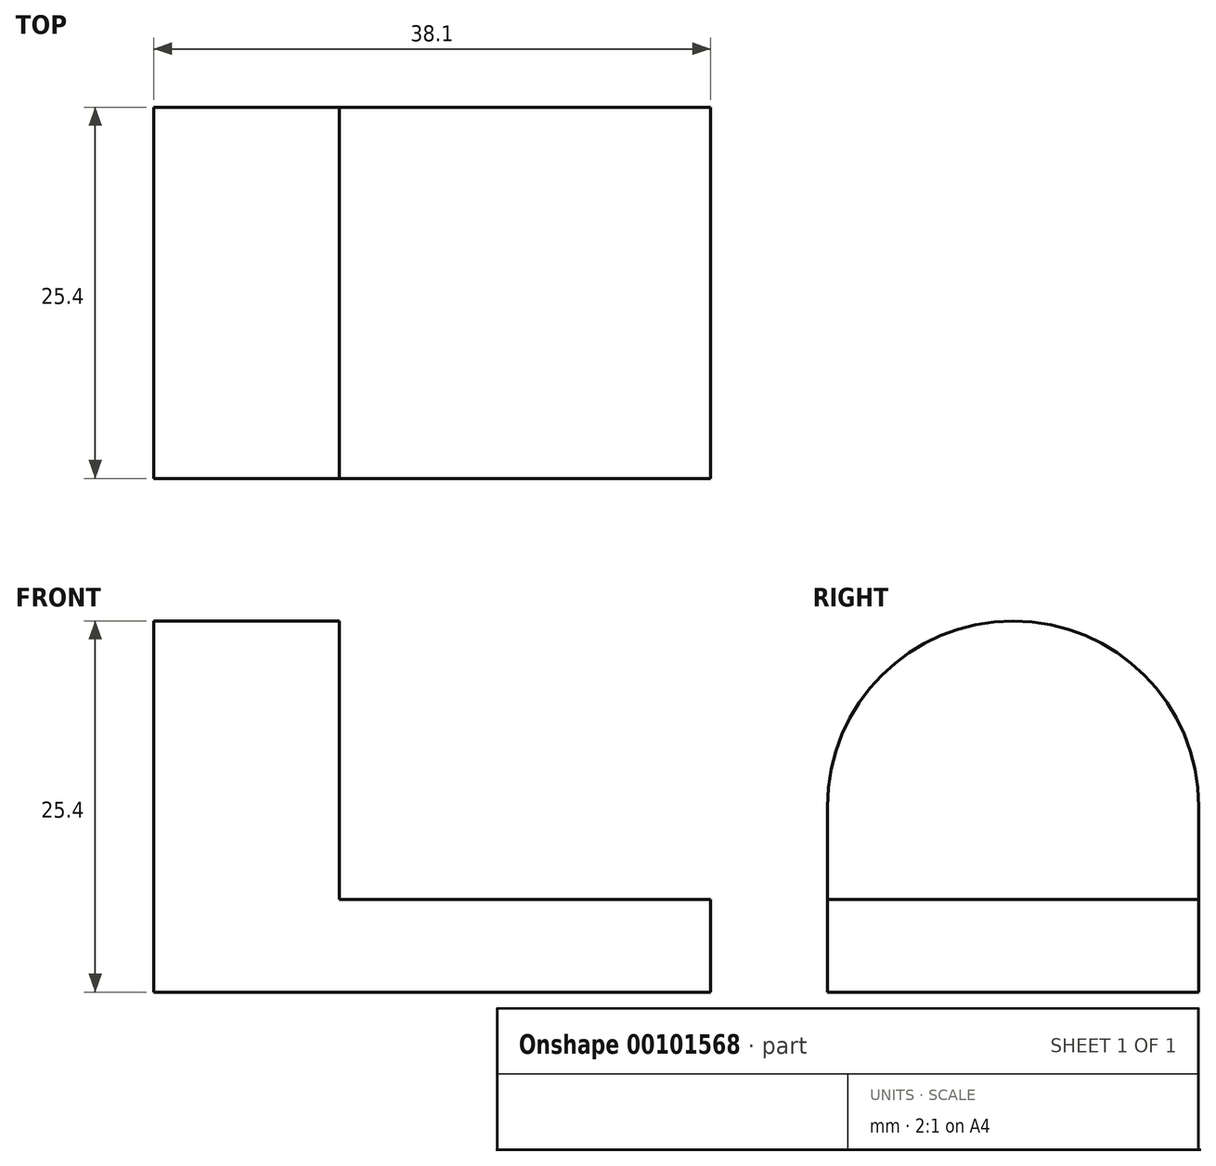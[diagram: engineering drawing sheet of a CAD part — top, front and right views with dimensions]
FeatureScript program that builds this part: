
annotation { "Feature Type Name" : "Feature", "Feature Type Description" : "" }
export const myFeature = defineFeature(function(context is Context, id is Id, definition is map)
    precondition{}
    {
        {
            var Q0;
            Q0=qCreatedBy(makeId("Front.planeOp"),FACE);
            var sketch = newSketch(context, id + "F0", { "sketchPlane" : qUnion([Q0])});
            skLineSegment(sketch, "E0", {"start": v(0, 0) * mm, "end": v(38.1, 0) * mm});
            skLineSegment(sketch, "E1", {"start": v(38.1, 0) * mm, "end": v(38.1, 6.35) * mm});
            skLineSegment(sketch, "E2", {"start": v(38.1, 6.35) * mm, "end": v(12.7, 6.35) * mm});
            skLineSegment(sketch, "E3", {"start": v(12.7, 6.35) * mm, "end": v(12.7, 25.4) * mm});
            skLineSegment(sketch, "E4", {"start": v(12.7, 25.4) * mm, "end": v(0, 25.4) * mm});
            skLineSegment(sketch, "E5", {"start": v(0, 25.4) * mm, "end": v(0, 0) * mm});
            skSolve(sketch);
        }
        {
            var Q0;
            Q0 = qSketchRegion(id + "F0", true);
            extrude(context, id + "F1", {"entities" : qUnion([Q0]), "oppositeDirection" : true, "depth" : 25.4 * mm});
        }
        {
            var Q0;
            Q0=makeQuery(id+"F1.opExtrude","CAP_EDGE",EDGE,{"disambiguationData":[OSD([sQuery(id+"F0.wireOp",EDGE,"E4")])],"isStart":true});
            var Q1;
            Q1=makeQuery(id+"F1.opExtrude","CAP_EDGE",EDGE,{"disambiguationData":[OSD([sQuery(id+"F0.wireOp",EDGE,"E4")])],"isStart":false});
            fillet(context, id + "F2", {"entities" : qUnion([Q0, Q1]), "radius" : 12.7 * mm, "tangentPropagation" : true, "allowEdgeOverflow" : false});
        }
    });
